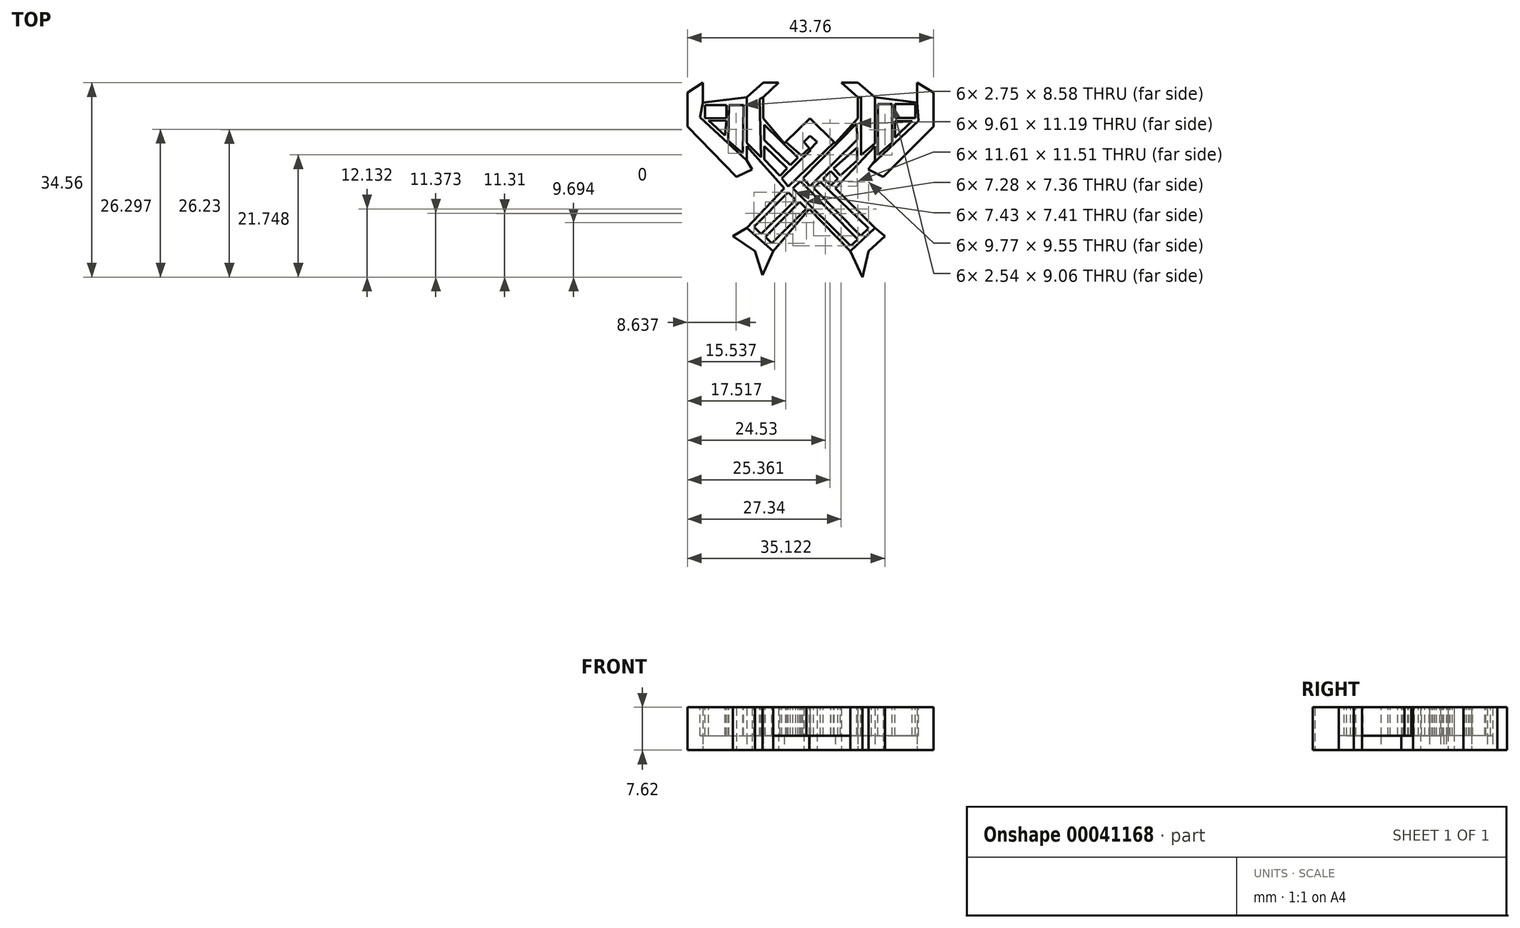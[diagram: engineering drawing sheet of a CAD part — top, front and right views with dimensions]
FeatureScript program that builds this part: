
annotation { "Feature Type Name" : "Feature", "Feature Type Description" : "" }
export const myFeature = defineFeature(function(context is Context, id is Id, definition is map)
    precondition{}
    {
        {
            var Q0;
            Q0=qCreatedBy(makeId("Top.planeOp"),FACE);
            var sketch = newSketch(context, id + "F0", { "sketchPlane" : qUnion([Q0])});
            skPoint(sketch, "E0", {"position": v(25.59, 35.04) * mm});
            skPoint(sketch, "E1", {"position": v(30.08, 30.56) * mm});
            skPoint(sketch, "E2", {"position": v(20.98, 30.56) * mm});
            skPoint(sketch, "E3", {"position": v(34.08, 35.04) * mm});
            skPoint(sketch, "E4", {"position": v(17.22, 35.04) * mm});
            skPoint(sketch, "E5", {"position": v(17.22, 38.8) * mm});
            skPoint(sketch, "E6", {"position": v(34.08, 38.8) * mm});
            skPoint(sketch, "E7", {"position": v(20.01, 41.35) * mm});
            skPoint(sketch, "E8", {"position": v(17.22, 41.35) * mm});
            skPoint(sketch, "E9", {"position": v(31.17, 41.35) * mm});
            skPoint(sketch, "E10", {"position": v(34.08, 41.35) * mm});
            skPoint(sketch, "E11", {"position": v(37.1, 38.8) * mm});
            skPoint(sketch, "E12", {"position": v(14.31, 38.8) * mm});
            skPoint(sketch, "E13", {"position": v(44.62, 37.83) * mm});
            skPoint(sketch, "E14", {"position": v(6.55, 37.83) * mm});
            skPoint(sketch, "E15", {"position": v(6.55, 41.35) * mm});
            skPoint(sketch, "E16", {"position": v(44.62, 41.35) * mm});
            skPoint(sketch, "E17", {"position": v(20.98, 22.55) * mm});
            skPoint(sketch, "E18", {"position": v(30.08, 22.55) * mm});
            skPoint(sketch, "E19", {"position": v(37.1, 30.07) * mm});
            skPoint(sketch, "E20", {"position": v(14.31, 30.07) * mm});
            skLineSegment(sketch, "E21", {"start": v(6.55, 41.35) * mm, "end": v(6.55, 37.83) * mm});
            skLineSegment(sketch, "E22", {"start": v(6.55, 37.83) * mm, "end": v(14.31, 38.8) * mm});
            skLineSegment(sketch, "E23", {"start": v(17.22, 41.35) * mm, "end": v(14.31, 38.8) * mm});
            skLineSegment(sketch, "E24", {"start": v(37.1, 38.8) * mm, "end": v(44.62, 37.83) * mm});
            skLineSegment(sketch, "E25", {"start": v(34.08, 41.35) * mm, "end": v(37.1, 38.8) * mm});
            skLineSegment(sketch, "E26", {"start": v(31.17, 41.35) * mm, "end": v(34.08, 41.35) * mm});
            skLineSegment(sketch, "E27", {"start": v(20.01, 41.35) * mm, "end": v(17.22, 41.35) * mm});
            skLineSegment(sketch, "E28", {"start": v(20.01, 41.35) * mm, "end": v(17.22, 38.8) * mm});
            skLineSegment(sketch, "E29", {"start": v(17.22, 38.8) * mm, "end": v(17.22, 35.04) * mm});
            skLineSegment(sketch, "E30", {"start": v(20.98, 30.56) * mm, "end": v(17.22, 35.04) * mm});
            skLineSegment(sketch, "E31", {"start": v(25.59, 35.04) * mm, "end": v(20.98, 30.56) * mm});
            skLineSegment(sketch, "E32", {"start": v(25.59, 35.04) * mm, "end": v(30.08, 30.56) * mm});
            skLineSegment(sketch, "E33", {"start": v(34.08, 35.04) * mm, "end": v(30.08, 30.56) * mm});
            skLineSegment(sketch, "E34", {"start": v(34.08, 38.8) * mm, "end": v(34.08, 35.04) * mm});
            skLineSegment(sketch, "E35", {"start": v(31.17, 41.35) * mm, "end": v(34.08, 38.8) * mm});
            skLineSegment(sketch, "E36", {"start": v(44.62, 41.35) * mm, "end": v(44.62, 37.83) * mm});
            skLineSegment(sketch, "E37", {"start": v(37.1, 30.07) * mm, "end": v(30.08, 22.55) * mm});
            skLineSegment(sketch, "E38", {"start": v(20.98, 22.55) * mm, "end": v(14.31, 30.07) * mm});
            skPoint(sketch, "E39", {"position": v(14.31, 27.52) * mm});
            skPoint(sketch, "E40", {"position": v(37.1, 27.52) * mm});
            skPoint(sketch, "E41", {"position": v(37.1, 15.52) * mm});
            skPoint(sketch, "E42", {"position": v(14.31, 15.52) * mm});
            skLineSegment(sketch, "E43", {"start": v(14.31, 27.52) * mm, "end": v(14.31, 30.07) * mm});
            skLineSegment(sketch, "E44", {"start": v(37.1, 27.52) * mm, "end": v(37.1, 30.07) * mm});
            skLineSegment(sketch, "E45", {"start": v(37.1, 15.52) * mm, "end": v(30.08, 22.55) * mm});
            skLineSegment(sketch, "E46", {"start": v(20.98, 22.55) * mm, "end": v(14.31, 15.52) * mm});
            skPoint(sketch, "E47", {"position": v(3.77, 33.59) * mm});
            skPoint(sketch, "E48", {"position": v(47.53, 33.59) * mm});
            skPoint(sketch, "E49", {"position": v(47.53, 39.59) * mm});
            skPoint(sketch, "E50", {"position": v(3.77, 39.59) * mm});
            skLineSegment(sketch, "E51", {"start": v(6.55, 41.35) * mm, "end": v(3.77, 39.59) * mm});
            skLineSegment(sketch, "E52", {"start": v(44.62, 41.35) * mm, "end": v(47.53, 39.59) * mm});
            skLineSegment(sketch, "E53", {"start": v(47.53, 39.59) * mm, "end": v(47.53, 33.59) * mm});
            skLineSegment(sketch, "E54", {"start": v(3.77, 39.59) * mm, "end": v(3.77, 33.59) * mm});
            skPoint(sketch, "E55", {"position": v(15.28, 25.95) * mm});
            skPoint(sketch, "E56", {"position": v(35.9, 25.95) * mm});
            skPoint(sketch, "E57", {"position": v(12.5, 24.61) * mm});
            skPoint(sketch, "E58", {"position": v(38.56, 24.61) * mm});
            skLineSegment(sketch, "E59", {"start": v(3.77, 33.59) * mm, "end": v(12.5, 24.61) * mm});
            skLineSegment(sketch, "E60", {"start": v(15.28, 25.95) * mm, "end": v(14.31, 27.52) * mm});
            skLineSegment(sketch, "E61", {"start": v(15.28, 25.95) * mm, "end": v(12.5, 24.61) * mm});
            skLineSegment(sketch, "E62", {"start": v(35.9, 25.95) * mm, "end": v(38.56, 24.61) * mm});
            skLineSegment(sketch, "E63", {"start": v(47.53, 33.59) * mm, "end": v(38.56, 24.61) * mm});
            skLineSegment(sketch, "E64", {"start": v(37.1, 27.52) * mm, "end": v(35.9, 25.95) * mm});
            skPoint(sketch, "E65", {"position": v(25.47, 18.92) * mm});
            skPoint(sketch, "E66", {"position": v(19.04, 11.4) * mm});
            skPoint(sketch, "E67", {"position": v(32.74, 11.4) * mm});
            skPoint(sketch, "E68", {"position": v(34.93, 6.8) * mm});
            skPoint(sketch, "E69", {"position": v(17.1, 7.16) * mm});
            skPoint(sketch, "E70", {"position": v(11.89, 14.07) * mm});
            skPoint(sketch, "E71", {"position": v(38.93, 14.07) * mm});
            skLineSegment(sketch, "E72", {"start": v(25.47, 18.92) * mm, "end": v(19.04, 11.4) * mm});
            skLineSegment(sketch, "E73", {"start": v(25.47, 18.92) * mm, "end": v(32.74, 11.4) * mm});
            skLineSegment(sketch, "E74", {"start": v(38.93, 14.07) * mm, "end": v(37.1, 15.52) * mm});
            skPoint(sketch, "E75", {"position": v(36.02, 11.4) * mm});
            skPoint(sketch, "E76", {"position": v(15.77, 11.4) * mm});
            skLineSegment(sketch, "E77", {"start": v(14.31, 15.52) * mm, "end": v(11.89, 14.07) * mm});
            skLineSegment(sketch, "E78", {"start": v(11.89, 14.07) * mm, "end": v(15.77, 11.4) * mm});
            skLineSegment(sketch, "E79", {"start": v(15.77, 11.4) * mm, "end": v(17.1, 7.16) * mm});
            skLineSegment(sketch, "E80", {"start": v(19.04, 11.4) * mm, "end": v(17.1, 7.16) * mm});
            skLineSegment(sketch, "E81", {"start": v(32.74, 11.4) * mm, "end": v(34.93, 6.8) * mm});
            skLineSegment(sketch, "E82", {"start": v(36.02, 11.4) * mm, "end": v(34.93, 6.8) * mm});
            skLineSegment(sketch, "E83", {"start": v(38.93, 14.07) * mm, "end": v(36.02, 11.4) * mm});
            skPoint(sketch, "E84", {"position": v(25.59, 31.9) * mm});
            skPoint(sketch, "E85", {"position": v(25.59, 29.51) * mm});
            skPoint(sketch, "E86", {"position": v(26.82, 30.83) * mm});
            skPoint(sketch, "E87", {"position": v(24.52, 30.83) * mm});
            skLineSegment(sketch, "E88", {"start": v(25.59, 31.9) * mm, "end": v(26.82, 30.83) * mm});
            skLineSegment(sketch, "E89", {"start": v(25.59, 31.9) * mm, "end": v(24.52, 30.83) * mm});
            skLineSegment(sketch, "E90", {"start": v(24.52, 30.83) * mm, "end": v(25.59, 29.51) * mm});
            skLineSegment(sketch, "E91", {"start": v(26.82, 30.83) * mm, "end": v(25.59, 29.51) * mm});
            skSolve(sketch);
        }
        {
            var Q0;
            Q0 = qSketchRegion(id + "F0", true);
            extrude(context, id + "F1", {"entities" : qUnion([Q0]), "depth" : 12.7 * mm});
        }
        {
            var Q0;
            Q0=makeQuery(id+"F1.opExtrude","CAP_FACE",FACE,{"disambiguationData":[OSD([sQuery(id+"F0.wireOp",EDGE,"E21"),sQuery(id+"F0.wireOp",EDGE,"E22"),sQuery(id+"F0.wireOp",EDGE,"E23"),sQuery(id+"F0.wireOp",EDGE,"E24"),sQuery(id+"F0.wireOp",EDGE,"E25"),sQuery(id+"F0.wireOp",EDGE,"E26"),sQuery(id+"F0.wireOp",EDGE,"E27"),sQuery(id+"F0.wireOp",EDGE,"E28"),sQuery(id+"F0.wireOp",EDGE,"E29"),sQuery(id+"F0.wireOp",EDGE,"E30"),sQuery(id+"F0.wireOp",EDGE,"E31"),sQuery(id+"F0.wireOp",EDGE,"E32"),sQuery(id+"F0.wireOp",EDGE,"E33"),sQuery(id+"F0.wireOp",EDGE,"E34"),sQuery(id+"F0.wireOp",EDGE,"E35"),sQuery(id+"F0.wireOp",EDGE,"E36"),sQuery(id+"F0.wireOp",EDGE,"E37"),sQuery(id+"F0.wireOp",EDGE,"E38"),sQuery(id+"F0.wireOp",EDGE,"E43"),sQuery(id+"F0.wireOp",EDGE,"E44"),sQuery(id+"F0.wireOp",EDGE,"E45"),sQuery(id+"F0.wireOp",EDGE,"E46"),sQuery(id+"F0.wireOp",EDGE,"E51"),sQuery(id+"F0.wireOp",EDGE,"E52"),sQuery(id+"F0.wireOp",EDGE,"E53"),sQuery(id+"F0.wireOp",EDGE,"E54"),sQuery(id+"F0.wireOp",EDGE,"E59"),sQuery(id+"F0.wireOp",EDGE,"E60"),sQuery(id+"F0.wireOp",EDGE,"E61"),sQuery(id+"F0.wireOp",EDGE,"E62"),sQuery(id+"F0.wireOp",EDGE,"E63"),sQuery(id+"F0.wireOp",EDGE,"E64"),sQuery(id+"F0.wireOp",EDGE,"E72"),sQuery(id+"F0.wireOp",EDGE,"E73"),sQuery(id+"F0.wireOp",EDGE,"E74"),sQuery(id+"F0.wireOp",EDGE,"E77"),sQuery(id+"F0.wireOp",EDGE,"E78"),sQuery(id+"F0.wireOp",EDGE,"E79"),sQuery(id+"F0.wireOp",EDGE,"E80"),sQuery(id+"F0.wireOp",EDGE,"E81"),sQuery(id+"F0.wireOp",EDGE,"E82"),sQuery(id+"F0.wireOp",EDGE,"E83"),sQuery(id+"F0.wireOp",EDGE,"E88"),sQuery(id+"F0.wireOp",EDGE,"E89"),sQuery(id+"F0.wireOp",EDGE,"E90"),sQuery(id+"F0.wireOp",EDGE,"E91")])],"isStart":false});
            var sketch = newSketch(context, id + "F2", { "sketchPlane" : qUnion([Q0])});
            skPoint(sketch, "E92", {"position": v(7.05, 37.9) * mm});
            skPoint(sketch, "E93", {"position": v(6.55, 37.83) * mm});
            skPoint(sketch, "E94", {"position": v(6.04, 35.23) * mm});
            skPoint(sketch, "E95", {"position": v(6.92, 35) * mm});
            skPoint(sketch, "E96", {"position": v(10.46, 32) * mm});
            skPoint(sketch, "E97", {"position": v(14.31, 27.52) * mm});
            skPoint(sketch, "E98", {"position": v(13.63, 28.8) * mm});
            skPoint(sketch, "E98.positionSnap0", {"position": v(14.31, 28.8) * mm});
            skPoint(sketch, "E99", {"position": v(7.52, 34.66) * mm});
            skPoint(sketch, "E100", {"position": v(10.7, 34.59) * mm});
            skPoint(sketch, "E101", {"position": v(10.7, 35.12) * mm});
            skPoint(sketch, "E102", {"position": v(10.7, 37.38) * mm});
            skPoint(sketch, "E103", {"position": v(6.92, 37.38) * mm});
            skLineSegment(sketch, "E104", {"start": v(6.55, 37.83) * mm, "end": v(6.04, 35.23) * mm});
            skLineSegment(sketch, "E105", {"start": v(6.55, 37.83) * mm, "end": v(7.05, 37.9) * mm});
            skLineSegment(sketch, "E106", {"start": v(6.92, 37.38) * mm, "end": v(10.7, 37.38) * mm});
            skLineSegment(sketch, "E107", {"start": v(6.92, 37.38) * mm, "end": v(6.92, 35) * mm});
            skLineSegment(sketch, "E108", {"start": v(10.7, 35.12) * mm, "end": v(6.92, 35) * mm});
            skLineSegment(sketch, "E109", {"start": v(10.7, 37.38) * mm, "end": v(10.7, 35.12) * mm});
            skLineSegment(sketch, "E110", {"start": v(10.7, 34.59) * mm, "end": v(10.46, 32) * mm});
            skLineSegment(sketch, "E111", {"start": v(7.52, 34.66) * mm, "end": v(10.46, 32) * mm});
            skLineSegment(sketch, "E112", {"start": v(7.52, 34.66) * mm, "end": v(10.7, 34.59) * mm});
            skPoint(sketch, "E113", {"position": v(11.17, 37.38) * mm});
            skPoint(sketch, "E114", {"position": v(13.78, 37.38) * mm});
            skPoint(sketch, "E115", {"position": v(14.19, 38.78) * mm});
            skPoint(sketch, "E116", {"position": v(11.03, 31.06) * mm});
            skLineSegment(sketch, "E117", {"start": v(11.03, 31.06) * mm, "end": v(13.63, 28.8) * mm});
            skLineSegment(sketch, "E118", {"start": v(11.17, 37.38) * mm, "end": v(11.03, 31.06) * mm});
            skLineSegment(sketch, "E119", {"start": v(11.17, 37.38) * mm, "end": v(13.78, 37.38) * mm});
            skLineSegment(sketch, "E120", {"start": v(13.78, 37.38) * mm, "end": v(13.63, 28.8) * mm});
            skLineSegment(sketch, "E121", {"start": v(6.04, 35.23) * mm, "end": v(14.31, 27.52) * mm});
            skPoint(sketch, "E122", {"position": v(25.7, 29.4) * mm});
            skPoint(sketch, "E123", {"position": v(25.42, 29.72) * mm});
            skPoint(sketch, "E124", {"position": v(24.08, 28.45) * mm});
            skPoint(sketch, "E125", {"position": v(21.26, 30.83) * mm});
            skPoint(sketch, "E126", {"position": v(29.87, 30.76) * mm});
            skPoint(sketch, "E127", {"position": v(20.53, 24.36) * mm});
            skPoint(sketch, "E128", {"position": v(21.72, 22.87) * mm});
            skLineSegment(sketch, "E129", {"start": v(25.59, 35.04) * mm, "end": v(21.26, 30.83) * mm});
            skLineSegment(sketch, "E130", {"start": v(25.59, 35.04) * mm, "end": v(26.38, 34.73) * mm});
            skLineSegment(sketch, "E131", {"start": v(25.59, 35.04) * mm, "end": v(29.87, 30.76) * mm});
            skLineSegment(sketch, "E132", {"start": v(21.26, 30.83) * mm, "end": v(24.08, 28.45) * mm});
            skLineSegment(sketch, "E133", {"start": v(25.42, 29.72) * mm, "end": v(24.08, 28.45) * mm});
            skLineSegment(sketch, "E134", {"start": v(29.87, 30.76) * mm, "end": v(21.72, 22.87) * mm});
            skLineSegment(sketch, "E135", {"start": v(25.7, 29.4) * mm, "end": v(20.53, 24.36) * mm});
            skLineSegment(sketch, "E136", {"start": v(25.59, 29.51) * mm, "end": v(25.7, 29.4) * mm});
            skLineSegment(sketch, "E137", {"start": v(20.53, 24.36) * mm, "end": v(21.72, 22.87) * mm});
            skLineSegment(sketch, "E138.bottom", {"start": v(40.68, 37.55) * mm, "end": v(44.33, 37.55) * mm});
            skLineSegment(sketch, "E138.top", {"start": v(40.68, 35.1) * mm, "end": v(44.33, 35.1) * mm});
            skLineSegment(sketch, "E138.left", {"start": v(40.68, 37.55) * mm, "end": v(40.68, 35.1) * mm});
            skLineSegment(sketch, "E138.right", {"start": v(44.33, 37.55) * mm, "end": v(44.33, 35.1) * mm});
            skPoint(sketch, "E139.firstSnap0", {"position": v(42.5, 37.55) * mm});
            skLineSegment(sketch, "E139.bottom", {"start": v(37.62, 37.55) * mm, "end": v(40.16, 37.55) * mm});
            skLineSegment(sketch, "E139.left", {"start": v(37.62, 37.55) * mm, "end": v(37.62, 30.73) * mm});
            skLineSegment(sketch, "E139.right", {"start": v(40.16, 37.55) * mm, "end": v(40.16, 30.73) * mm});
            skLineSegment(sketch, "E140.left", {"start": v(34.65, 38.8) * mm, "end": v(34.65, 30.57) * mm});
            skLineSegment(sketch, "E140.right", {"start": v(37.1, 38.8) * mm, "end": v(37.1, 30.57) * mm});
            skPoint(sketch, "E141", {"position": v(40.68, 34.53) * mm});
            skPoint(sketch, "E142", {"position": v(43.73, 34.56) * mm});
            skPoint(sketch, "E143", {"position": v(40.68, 31.59) * mm});
            skLineSegment(sketch, "E144", {"start": v(43.73, 34.56) * mm, "end": v(40.68, 31.59) * mm});
            skLineSegment(sketch, "E145", {"start": v(40.68, 34.53) * mm, "end": v(40.68, 31.59) * mm});
            skLineSegment(sketch, "E146", {"start": v(43.73, 34.56) * mm, "end": v(40.68, 34.53) * mm});
            skPoint(sketch, "E147", {"position": v(44.9, 34.56) * mm});
            skPoint(sketch, "E148", {"position": v(36.5, 26.74) * mm});
            skLineSegment(sketch, "E149", {"start": v(44.62, 37.83) * mm, "end": v(44.9, 34.56) * mm});
            skLineSegment(sketch, "E150", {"start": v(44.9, 34.56) * mm, "end": v(36.5, 26.74) * mm});
            skPoint(sketch, "E151", {"position": v(14.31, 30.88) * mm});
            skPoint(sketch, "E152", {"position": v(16.88, 28.12) * mm});
            skPoint(sketch, "E153", {"position": v(16.64, 38.43) * mm});
            skLineSegment(sketch, "E154", {"start": v(16.64, 38.43) * mm, "end": v(17.22, 38.8) * mm});
            skLineSegment(sketch, "E155", {"start": v(17.22, 38.8) * mm, "end": v(20.01, 41.35) * mm});
            skLineSegment(sketch, "E156", {"start": v(20.01, 41.35) * mm, "end": v(17.22, 41.35) * mm});
            skLineSegment(sketch, "E157", {"start": v(17.22, 41.35) * mm, "end": v(14.31, 38.8) * mm});
            skLineSegment(sketch, "E158", {"start": v(14.31, 38.8) * mm, "end": v(14.31, 30.62) * mm});
            skLineSegment(sketch, "E159", {"start": v(14.31, 30.62) * mm, "end": v(16.88, 28.12) * mm});
            skLineSegment(sketch, "E160", {"start": v(16.64, 38.43) * mm, "end": v(16.88, 28.12) * mm});
            skLineSegment(sketch, "E161", {"start": v(34.65, 38.8) * mm, "end": v(34.08, 38.8) * mm});
            skLineSegment(sketch, "E162", {"start": v(34.08, 38.8) * mm, "end": v(31.17, 41.35) * mm});
            skLineSegment(sketch, "E163", {"start": v(31.17, 41.35) * mm, "end": v(34.08, 41.35) * mm});
            skLineSegment(sketch, "E164", {"start": v(34.08, 41.35) * mm, "end": v(37.1, 38.8) * mm});
            skPoint(sketch, "E165", {"position": v(34.65, 28.49) * mm});
            skPoint(sketch, "E166", {"position": v(37.62, 28.49) * mm});
            skLineSegment(sketch, "E167", {"start": v(37.62, 30.73) * mm, "end": v(37.62, 28.49) * mm});
            skLineSegment(sketch, "E168", {"start": v(40.16, 30.73) * mm, "end": v(37.62, 28.49) * mm});
            skLineSegment(sketch, "E169", {"start": v(37.1, 30.57) * mm, "end": v(34.65, 28.49) * mm});
            skLineSegment(sketch, "E170", {"start": v(34.65, 30.57) * mm, "end": v(34.65, 28.49) * mm});
            skPoint(sketch, "E171", {"position": v(22.06, 26.72) * mm});
            skPoint(sketch, "E172", {"position": v(23.45, 28.02) * mm});
            skPoint(sketch, "E173", {"position": v(17.47, 33.85) * mm});
            skPoint(sketch, "E174", {"position": v(17.47, 31.14) * mm});
            skPoint(sketch, "E175", {"position": v(17.47, 30.1) * mm});
            skPoint(sketch, "E176", {"position": v(17.47, 27.7) * mm});
            skPoint(sketch, "E177", {"position": v(20.25, 24.77) * mm});
            skLineSegment(sketch, "E178", {"start": v(17.47, 33.85) * mm, "end": v(17.47, 31.14) * mm});
            skLineSegment(sketch, "E179", {"start": v(17.47, 30.1) * mm, "end": v(17.47, 27.7) * mm});
            skLineSegment(sketch, "E180", {"start": v(17.47, 31.14) * mm, "end": v(22.06, 26.72) * mm});
            skLineSegment(sketch, "E181", {"start": v(23.45, 28.02) * mm, "end": v(22.06, 26.72) * mm});
            skLineSegment(sketch, "E182", {"start": v(17.47, 33.85) * mm, "end": v(23.45, 28.02) * mm});
            skPoint(sketch, "E183", {"position": v(21.48, 26.14) * mm});
            skLineSegment(sketch, "E184", {"start": v(21.48, 26.14) * mm, "end": v(20.25, 24.77) * mm});
            skLineSegment(sketch, "E185", {"start": v(17.47, 27.7) * mm, "end": v(20.25, 24.77) * mm});
            skLineSegment(sketch, "E186", {"start": v(17.47, 30.1) * mm, "end": v(21.48, 26.14) * mm});
            skLineSegment(sketch, "E187", {"start": v(37.1, 38.8) * mm, "end": v(44.62, 37.83) * mm});
            skLineSegment(sketch, "E188", {"start": v(34.08, 38.8) * mm, "end": v(34.08, 35.04) * mm});
            skLineSegment(sketch, "E189", {"start": v(34.08, 35.04) * mm, "end": v(30.08, 30.56) * mm});
            skLineSegment(sketch, "E190", {"start": v(30.08, 30.56) * mm, "end": v(29.87, 30.76) * mm});
            skLineSegment(sketch, "E191", {"start": v(21.26, 30.83) * mm, "end": v(20.98, 30.56) * mm});
            skLineSegment(sketch, "E192", {"start": v(20.98, 30.56) * mm, "end": v(17.22, 35.04) * mm});
            skLineSegment(sketch, "E193", {"start": v(17.22, 35.04) * mm, "end": v(17.22, 38.8) * mm});
            skLineSegment(sketch, "E194", {"start": v(14.31, 38.8) * mm, "end": v(6.55, 37.83) * mm});
            skPoint(sketch, "E195", {"position": v(25.59, 22.95) * mm});
            skPoint(sketch, "E196", {"position": v(24.33, 24.36) * mm});
            skPoint(sketch, "E197", {"position": v(33.94, 31.23) * mm});
            skPoint(sketch, "E198", {"position": v(33.9, 34.13) * mm});
            skPoint(sketch, "E199", {"position": v(29.26, 25.6) * mm});
            skPoint(sketch, "E200", {"position": v(30.51, 24.29) * mm});
            skPoint(sketch, "E201", {"position": v(29.33, 23.1) * mm});
            skPoint(sketch, "E202", {"position": v(27.91, 24.29) * mm});
            skPoint(sketch, "E203", {"position": v(31, 24.89) * mm});
            skPoint(sketch, "E204", {"position": v(29.74, 26.15) * mm});
            skPoint(sketch, "E205", {"position": v(33.94, 27.51) * mm});
            skPoint(sketch, "E206", {"position": v(33.94, 29.84) * mm});
            skLineSegment(sketch, "E207", {"start": v(33.9, 34.13) * mm, "end": v(24.33, 24.36) * mm});
            skLineSegment(sketch, "E208", {"start": v(33.9, 34.13) * mm, "end": v(33.94, 31.23) * mm});
            skLineSegment(sketch, "E209", {"start": v(33.94, 31.23) * mm, "end": v(25.59, 22.95) * mm});
            skLineSegment(sketch, "E210", {"start": v(24.33, 24.36) * mm, "end": v(25.59, 22.95) * mm});
            skLineSegment(sketch, "E211", {"start": v(29.26, 25.6) * mm, "end": v(27.91, 24.29) * mm});
            skLineSegment(sketch, "E212", {"start": v(29.26, 25.6) * mm, "end": v(30.51, 24.29) * mm});
            skLineSegment(sketch, "E213", {"start": v(30.51, 24.29) * mm, "end": v(29.33, 23.1) * mm});
            skLineSegment(sketch, "E214", {"start": v(27.91, 24.29) * mm, "end": v(29.33, 23.1) * mm});
            skLineSegment(sketch, "E215", {"start": v(29.74, 26.15) * mm, "end": v(31, 24.89) * mm});
            skLineSegment(sketch, "E216", {"start": v(33.94, 27.51) * mm, "end": v(31, 24.89) * mm});
            skLineSegment(sketch, "E217", {"start": v(33.94, 29.84) * mm, "end": v(33.94, 27.51) * mm});
            skLineSegment(sketch, "E218", {"start": v(29.74, 26.15) * mm, "end": v(33.94, 29.84) * mm});
            skLineSegment(sketch, "E219", {"start": v(14.31, 15.52) * mm, "end": v(19.04, 11.4) * mm});
            skLineSegment(sketch, "E220", {"start": v(19.04, 11.4) * mm, "end": v(25.47, 18.92) * mm});
            skLineSegment(sketch, "E221", {"start": v(25.47, 18.92) * mm, "end": v(32.74, 11.4) * mm});
            skLineSegment(sketch, "E222", {"start": v(32.74, 11.4) * mm, "end": v(37.1, 15.52) * mm});
            skLineSegment(sketch, "E223", {"start": v(37.1, 15.52) * mm, "end": v(30.08, 22.55) * mm});
            skLineSegment(sketch, "E224", {"start": v(30.08, 22.55) * mm, "end": v(37.1, 30.07) * mm});
            skLineSegment(sketch, "E225", {"start": v(37.1, 30.07) * mm, "end": v(37.1, 27.52) * mm});
            skLineSegment(sketch, "E226", {"start": v(37.1, 27.52) * mm, "end": v(36.5, 26.74) * mm});
            skLineSegment(sketch, "E227", {"start": v(14.31, 30.07) * mm, "end": v(14.31, 27.52) * mm});
            skLineSegment(sketch, "E228", {"start": v(14.31, 30.07) * mm, "end": v(20.98, 22.55) * mm});
            skLineSegment(sketch, "E229", {"start": v(20.98, 22.55) * mm, "end": v(14.31, 15.52) * mm});
            skPoint(sketch, "E230", {"position": v(23.85, 23.85) * mm});
            skPoint(sketch, "E231", {"position": v(22.5, 22.58) * mm});
            skPoint(sketch, "E232", {"position": v(34.1, 13.49) * mm});
            skPoint(sketch, "E233", {"position": v(32.78, 12.35) * mm});
            skPoint(sketch, "E234", {"position": v(34.6, 14.15) * mm});
            skPoint(sketch, "E235", {"position": v(36, 15.47) * mm});
            skPoint(sketch, "E236", {"position": v(27.45, 23.7) * mm});
            skPoint(sketch, "E236.positionSnap0", {"position": v(28.62, 23.7) * mm});
            skPoint(sketch, "E237", {"position": v(26.23, 22.65) * mm});
            skLineSegment(sketch, "E238", {"start": v(22.5, 22.58) * mm, "end": v(32.78, 12.35) * mm});
            skLineSegment(sketch, "E239", {"start": v(34.1, 13.49) * mm, "end": v(32.78, 12.35) * mm});
            skLineSegment(sketch, "E240", {"start": v(34.1, 13.49) * mm, "end": v(23.85, 23.85) * mm});
            skLineSegment(sketch, "E241", {"start": v(23.85, 23.85) * mm, "end": v(22.5, 22.58) * mm});
            skLineSegment(sketch, "E242", {"start": v(27.45, 23.7) * mm, "end": v(36, 15.47) * mm});
            skLineSegment(sketch, "E243", {"start": v(27.45, 23.7) * mm, "end": v(26.23, 22.65) * mm});
            skLineSegment(sketch, "E244", {"start": v(26.23, 22.65) * mm, "end": v(34.6, 14.15) * mm});
            skLineSegment(sketch, "E245", {"start": v(36, 15.47) * mm, "end": v(34.6, 14.15) * mm});
            skLineSegment(sketch, "E246", {"start": v(21.72, 21.87) * mm, "end": v(23.02, 20.55) * mm});
            skLineSegment(sketch, "E247", {"start": v(23.02, 20.55) * mm, "end": v(16.86, 14.46) * mm});
            skLineSegment(sketch, "E248", {"start": v(16.86, 14.46) * mm, "end": v(15.6, 15.74) * mm});
            skLineSegment(sketch, "E249", {"start": v(15.6, 15.74) * mm, "end": v(21.72, 21.87) * mm});
            skLineSegment(sketch, "E250", {"start": v(23.71, 20.17) * mm, "end": v(24.93, 18.96) * mm});
            skLineSegment(sketch, "E251", {"start": v(24.93, 18.96) * mm, "end": v(18.8, 12.8) * mm});
            skLineSegment(sketch, "E252", {"start": v(18.8, 12.8) * mm, "end": v(17.65, 13.96) * mm});
            skLineSegment(sketch, "E253", {"start": v(17.65, 13.96) * mm, "end": v(23.71, 20.17) * mm});
            skSolve(sketch);
        }
        {
            var Q0;
            {var subQ4=sQuery(id+"F2.wireOp",EDGE,"E104");Q0=makeQuery(id+"F2.imprint","IMPRINT",FACE,{"disambiguationData":[TD([[makeQuery(id+"F2.imprint","IMPRINT",EDGE,{"derivedFrom":subQ4}),1.0]])]});}
            extrude(context, id + "F3", {"entities" : qUnion([Q0]), "operationType" : NewBodyOperationType.REMOVE, "oppositeDirection" : true, "depth" : 5.08 * mm});
        }
        {
            var Q0;
            Q0=makeQuery(id+"F1.opExtrude","CAP_FACE",FACE,{"disambiguationData":[OSD([sQuery(id+"F0.wireOp",EDGE,"E21"),sQuery(id+"F0.wireOp",EDGE,"E22"),sQuery(id+"F0.wireOp",EDGE,"E23"),sQuery(id+"F0.wireOp",EDGE,"E24"),sQuery(id+"F0.wireOp",EDGE,"E25"),sQuery(id+"F0.wireOp",EDGE,"E26"),sQuery(id+"F0.wireOp",EDGE,"E27"),sQuery(id+"F0.wireOp",EDGE,"E28"),sQuery(id+"F0.wireOp",EDGE,"E29"),sQuery(id+"F0.wireOp",EDGE,"E30"),sQuery(id+"F0.wireOp",EDGE,"E31"),sQuery(id+"F0.wireOp",EDGE,"E32"),sQuery(id+"F0.wireOp",EDGE,"E33"),sQuery(id+"F0.wireOp",EDGE,"E34"),sQuery(id+"F0.wireOp",EDGE,"E35"),sQuery(id+"F0.wireOp",EDGE,"E36"),sQuery(id+"F0.wireOp",EDGE,"E37"),sQuery(id+"F0.wireOp",EDGE,"E38"),sQuery(id+"F0.wireOp",EDGE,"E43"),sQuery(id+"F0.wireOp",EDGE,"E44"),sQuery(id+"F0.wireOp",EDGE,"E45"),sQuery(id+"F0.wireOp",EDGE,"E46"),sQuery(id+"F0.wireOp",EDGE,"E51"),sQuery(id+"F0.wireOp",EDGE,"E52"),sQuery(id+"F0.wireOp",EDGE,"E53"),sQuery(id+"F0.wireOp",EDGE,"E54"),sQuery(id+"F0.wireOp",EDGE,"E59"),sQuery(id+"F0.wireOp",EDGE,"E60"),sQuery(id+"F0.wireOp",EDGE,"E61"),sQuery(id+"F0.wireOp",EDGE,"E62"),sQuery(id+"F0.wireOp",EDGE,"E63"),sQuery(id+"F0.wireOp",EDGE,"E64"),sQuery(id+"F0.wireOp",EDGE,"E72"),sQuery(id+"F0.wireOp",EDGE,"E73"),sQuery(id+"F0.wireOp",EDGE,"E74"),sQuery(id+"F0.wireOp",EDGE,"E77"),sQuery(id+"F0.wireOp",EDGE,"E78"),sQuery(id+"F0.wireOp",EDGE,"E79"),sQuery(id+"F0.wireOp",EDGE,"E80"),sQuery(id+"F0.wireOp",EDGE,"E81"),sQuery(id+"F0.wireOp",EDGE,"E82"),sQuery(id+"F0.wireOp",EDGE,"E83"),sQuery(id+"F0.wireOp",EDGE,"E88"),sQuery(id+"F0.wireOp",EDGE,"E89"),sQuery(id+"F0.wireOp",EDGE,"E90"),sQuery(id+"F0.wireOp",EDGE,"E91")])],"isStart":true});
            extrude(context, id + "F4", {"entities" : qUnion([Q0]), "operationType" : NewBodyOperationType.REMOVE, "oppositeDirection" : true, "depth" : 5.08 * mm});
        }
    });
